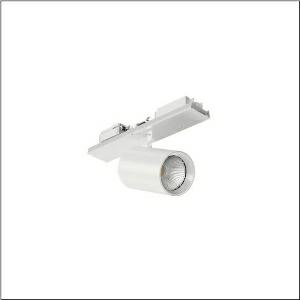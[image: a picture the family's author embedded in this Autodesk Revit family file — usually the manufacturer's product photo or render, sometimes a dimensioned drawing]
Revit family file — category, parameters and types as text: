
# Revit family: licross_spot_31_51sl147a45b
name_source: partatom
category: Lighting Fixtures
units: mm (PartAtom-declared; Revit-internal decimal feet)

## family parameters
Cut with Voids When Loaded = No
Host = Face
Light Source = No
Part Type = Normal
Room Calculation Point = No
Round Connector Dimension = Use Diameter
Shared = No

## types (1)
- --- (1 x LED, 5250 lm, 42.4 W, 4000K)
    Apparent Load = 42 VA
    CIE Flux Codes = 93 97 100 100 100
    Color Rendering = 90
    Color Temperature = 4000K
    Default Elevation = 1800 mm
    Description = Licross Spot 31, directional spotlight, light control with lens, of plastic, LED rated luminous flux: 5.250lm, light colour: 940, with plug, 3-pole, with phase selection, mains connection: 220..240V, AC, 50/60Hz, of aluminium, traffic white (RAL 9016), length: 300mm, diameter: 90mm, protection rating (complete): IP20, insulation class (complete): insulation class I (protective earthing), certification: CE, packaging unit: 1 piece
    Height = 175 mm
    Lamp = 1 x LED
    Lamp Light Flux = 5250 lm
    Lamp Power = 42.4 W
    Lamp count = 1
    Length = 90 mm
    Luminous efficacy = 124 lm/W
    Manufacturer = Siteco
    ModVariant = No
    Model = 51SL147A45B
    Mounting Place = Ceiling
    Mounting Type = Pendant
    Number of Poles = 1
    OnlyDefault = Yes
    Power Factor = 1
    Product Name = Licross Spot 31
    Product group = directional spotlight
    ProductGroupID = 905
    Protection Class = Protection class I
    Protection Degree = IP 20
    RLX_Detail_Level = 1
    RLX_Emergency_Light_Flux = 0 lm
    RLX_Emergency_Type = 0
    RLX_Emergency_Type_DB = No
    RlxData = <blob elided: 14781 chars, md5=3b511a4f>
    Socket = socket
    Standby Power = 0 W
    System Light Flux = 5250 lm
    System Power = 42 W
    Type Comments = factory setting: luminous flux: 100 % | (ON | ON | ON) | 1050 mA
    Type Image = l_1245720.jpg
    URL = http://relux.com
    VarID = @adj_131481
    Voltage = 0 V
    Weight = 0.00 kg
    Width = 0 mm  [stored 0 ft]

note: [stored X ft] marks values corroborated as IEEE doubles in the binary element streams (Revit-internal decimal feet)

## geometry (parser evidence)
native form markers: Sweep x10
no freeform markers — native parametric forms only
